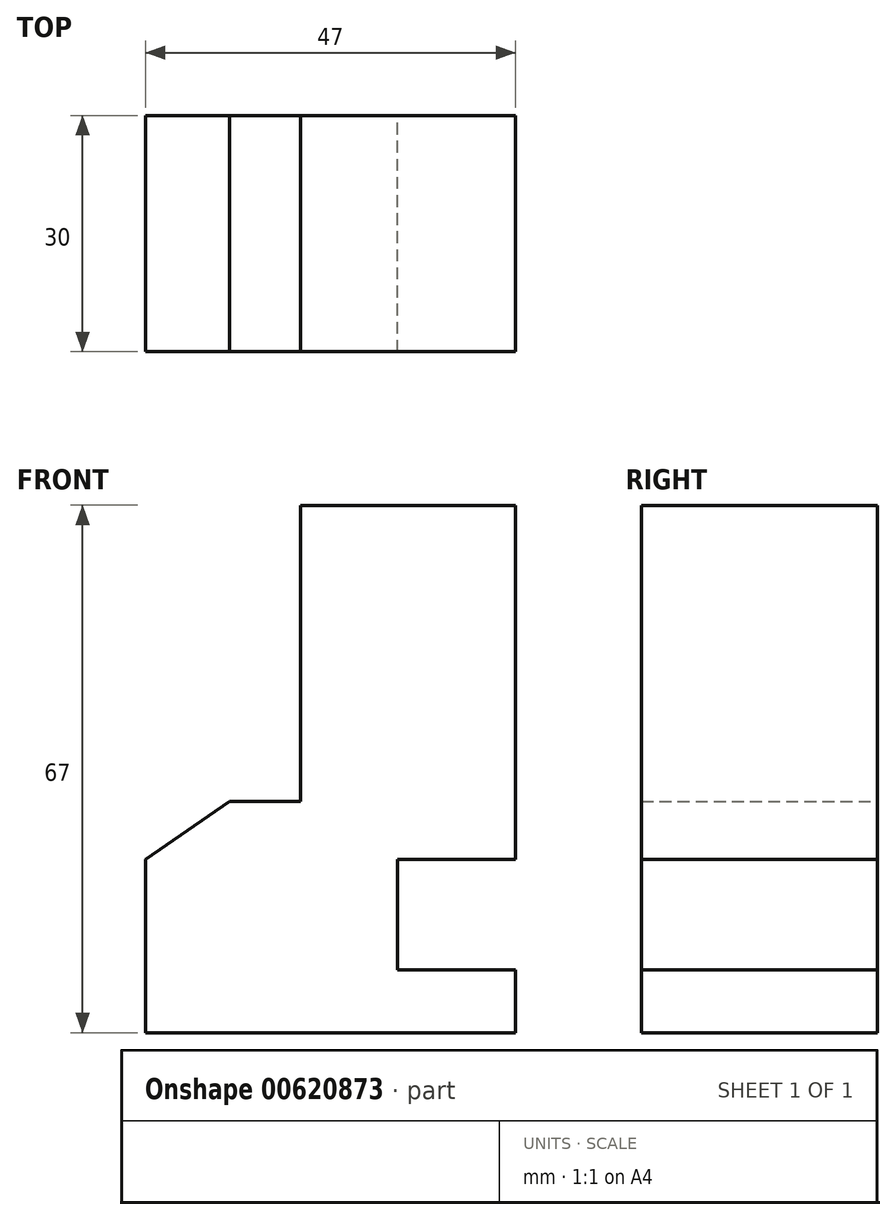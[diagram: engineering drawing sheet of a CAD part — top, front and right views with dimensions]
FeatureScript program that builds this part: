
annotation { "Feature Type Name" : "Feature", "Feature Type Description" : "" }
export const myFeature = defineFeature(function(context is Context, id is Id, definition is map)
    precondition{}
    {
        {
            var Q0;
            Q0=qCreatedBy(makeId("Front.planeOp"),FACE);
            var sketch = newSketch(context, id + "F0", { "sketchPlane" : qUnion([Q0])});
            skLineSegment(sketch, "E0", {"start": v(-12.31, 28.27) * mm, "end": v(15, 28.27) * mm});
            skLineSegment(sketch, "E1", {"start": v(15, 28.27) * mm, "end": v(15, -16.73) * mm});
            skLineSegment(sketch, "E2", {"start": v(15, -16.73) * mm, "end": v(0, -16.73) * mm});
            skLineSegment(sketch, "E3", {"start": v(0, -16.73) * mm, "end": v(0, -30.73) * mm});
            skLineSegment(sketch, "E4", {"start": v(0, -30.73) * mm, "end": v(15, -30.73) * mm});
            skLineSegment(sketch, "E5", {"start": v(15, -30.73) * mm, "end": v(15, -38.73) * mm});
            skLineSegment(sketch, "E6", {"start": v(15, -38.73) * mm, "end": v(-32, -38.73) * mm});
            skLineSegment(sketch, "E7", {"start": v(-32, -38.73) * mm, "end": v(-32, -16.73) * mm});
            skLineSegment(sketch, "E8", {"start": v(-32, -16.73) * mm, "end": v(-21.31, -9.33) * mm});
            skLineSegment(sketch, "E9", {"start": v(-21.31, -9.33) * mm, "end": v(-12.31, -9.33) * mm});
            skLineSegment(sketch, "E10", {"start": v(-12.31, -9.33) * mm, "end": v(-12.31, 28.27) * mm});
            skSolve(sketch);
        }
        {
            var Q0;
            Q0=makeQuery(id+"F0.imprint","IMPRINT",FACE,{"disambiguationData":[TD([[makeQuery(id+"F0.imprint","IMPRINT",EDGE,{"derivedFrom":sQuery(id+"F0.wireOp",EDGE,"E0")}),-1.0]])]});
            extrude(context, id + "F1", {"entities" : qUnion([Q0]), "depth" : 30 * mm, "offsetDistance" : 25 * mm});
        }
    });
